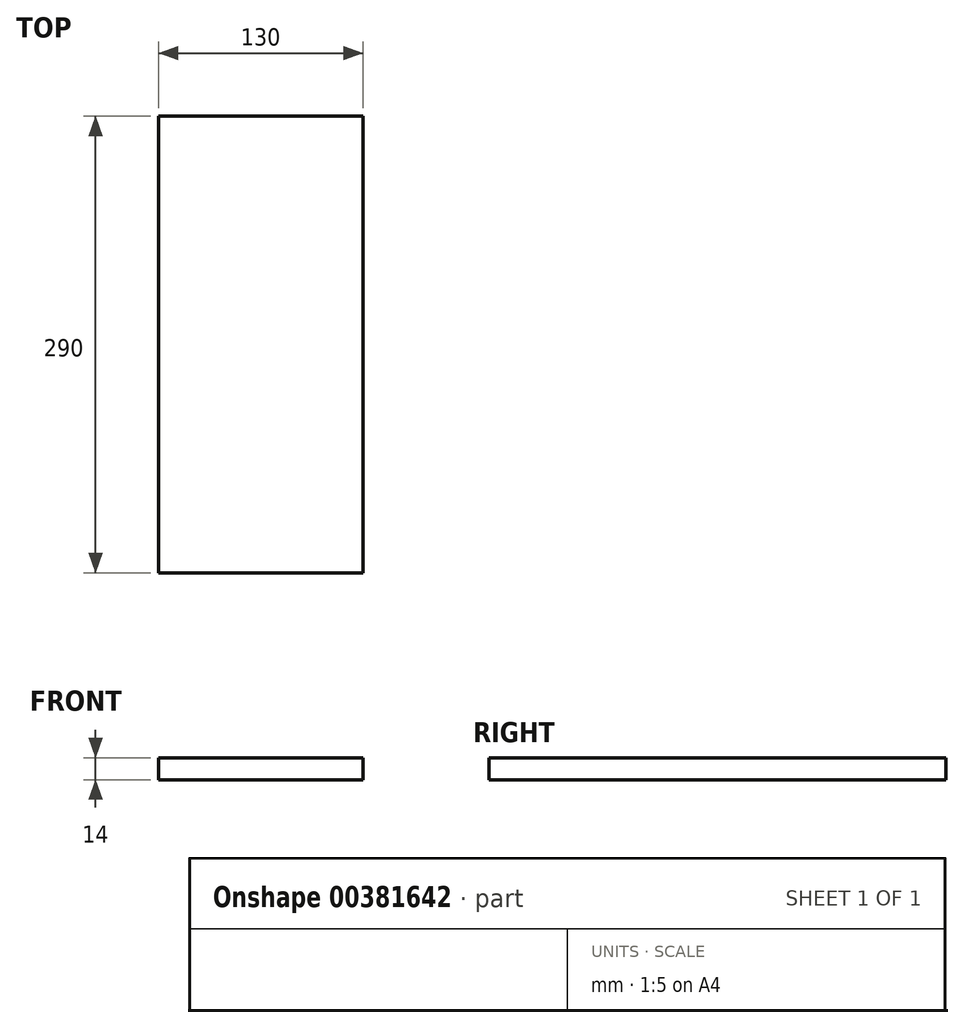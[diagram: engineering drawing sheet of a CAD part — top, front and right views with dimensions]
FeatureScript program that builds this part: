
annotation { "Feature Type Name" : "Feature", "Feature Type Description" : "" }
export const myFeature = defineFeature(function(context is Context, id is Id, definition is map)
    precondition{}
    {
        {
            var Q0;
            Q0=qCreatedBy(makeId("Top.planeOp"),FACE);
            var sketch = newSketch(context, id + "F0", { "sketchPlane" : qUnion([Q0])});
            skLineSegment(sketch, "E0.bottom", {"start": v(-57.13, 140.25) * mm, "end": v(72.87, 140.25) * mm});
            skLineSegment(sketch, "E0.top", {"start": v(-57.13, -149.75) * mm, "end": v(72.87, -149.75) * mm});
            skLineSegment(sketch, "E0.left", {"start": v(-57.13, 140.25) * mm, "end": v(-57.13, -149.75) * mm});
            skLineSegment(sketch, "E0.right", {"start": v(72.87, 140.25) * mm, "end": v(72.87, -149.75) * mm});
            skSolve(sketch);
        }
        {
            var Q0;
            Q0=makeQuery(id+"F0.imprint","IMPRINT",FACE,{"disambiguationData":[TD([[makeQuery(id+"F0.imprint","IMPRINT",EDGE,{"derivedFrom":sQuery(id+"F0.wireOp",EDGE,"E0.bottom")}),-1.0]])]});
            extrude(context, id + "F1", {"entities" : qUnion([Q0]), "depth" : 14 * mm});
        }
    });
